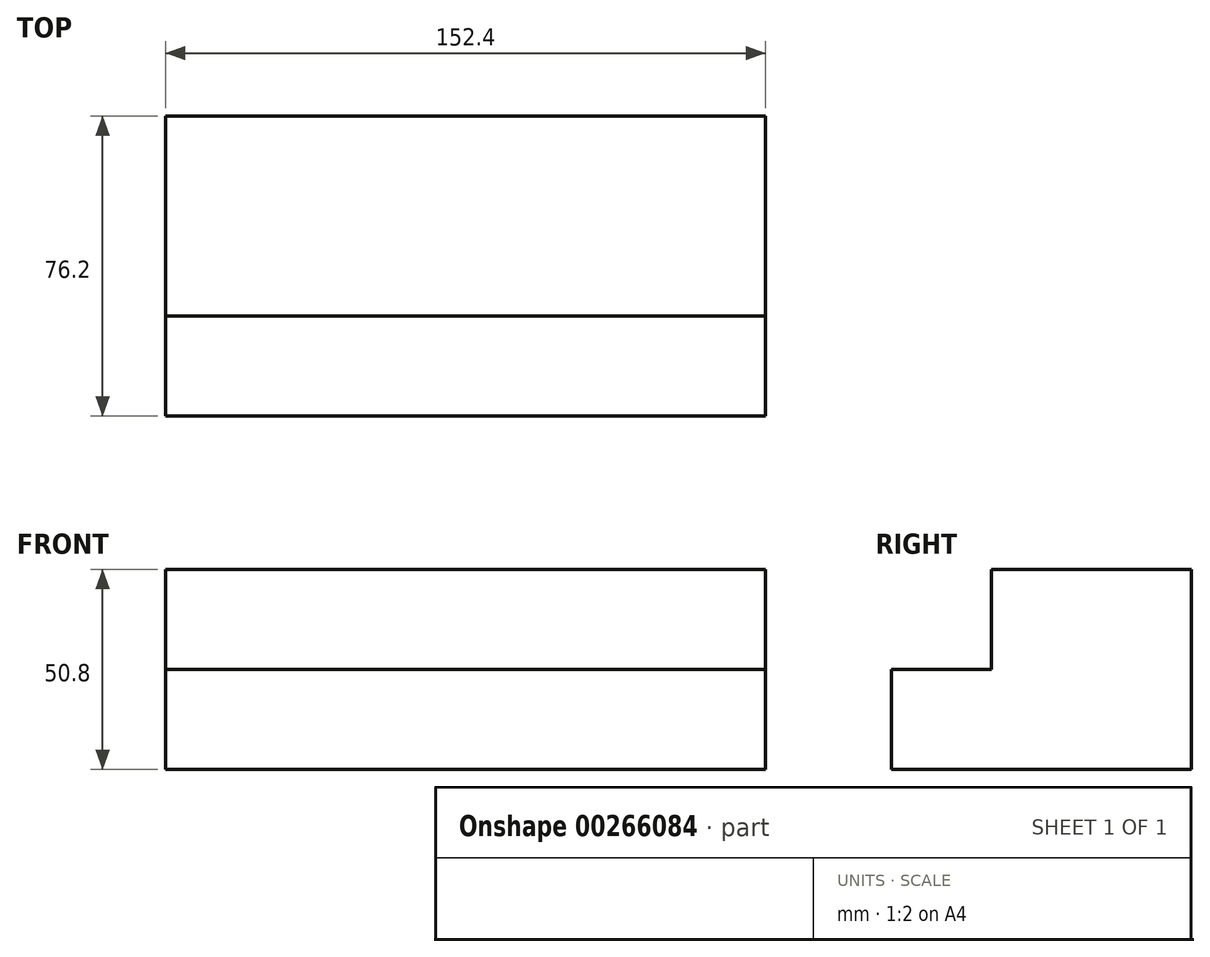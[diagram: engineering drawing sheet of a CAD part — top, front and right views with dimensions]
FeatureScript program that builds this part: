
annotation { "Feature Type Name" : "Feature", "Feature Type Description" : "" }
export const myFeature = defineFeature(function(context is Context, id is Id, definition is map)
    precondition{}
    {
        {
            var Q0;
            Q0=qCreatedBy(makeId("Right.planeOp"),FACE);
            var sketch = newSketch(context, id + "F0", { "sketchPlane" : qUnion([Q0])});
            skLineSegment(sketch, "E0.bottom", {"start": v(0, 0) * mm, "end": v(76.2, 0) * mm});
            skLineSegment(sketch, "E0.top", {"start": v(0, 50.8) * mm, "end": v(76.2, 50.8) * mm});
            skLineSegment(sketch, "E0.left", {"start": v(0, 0) * mm, "end": v(0, 50.8) * mm});
            skLineSegment(sketch, "E0.right", {"start": v(76.2, 0) * mm, "end": v(76.2, 50.8) * mm});
            skSolve(sketch);
        }
        {
            var Q0;
            Q0=makeQuery(id+"F0.imprint","IMPRINT",FACE,{"disambiguationData":[TD([[makeQuery(id+"F0.imprint","IMPRINT",EDGE,{"derivedFrom":sQuery(id+"F0.wireOp",EDGE,"E0.bottom")}),1.0]])]});
            extrude(context, id + "F1", {"entities" : qUnion([Q0]), "depth" : 152.4 * mm});
        }
        {
            var Q0;
            Q0=makeQuery(id+"F1.opExtrude","CAP_FACE",FACE,{"disambiguationData":[OSD([sQuery(id+"F0.wireOp",EDGE,"E0.bottom"),sQuery(id+"F0.wireOp",EDGE,"E0.top"),sQuery(id+"F0.wireOp",EDGE,"E0.left"),sQuery(id+"F0.wireOp",EDGE,"E0.right")])],"isStart":false});
            var sketch = newSketch(context, id + "F2", { "sketchPlane" : qUnion([Q0])});
            skLineSegment(sketch, "E1.bottom", {"start": v(0, 50.8) * mm, "end": v(25.4, 50.8) * mm});
            skLineSegment(sketch, "E1.top", {"start": v(0, 25.4) * mm, "end": v(25.4, 25.4) * mm});
            skLineSegment(sketch, "E1.left", {"start": v(0, 50.8) * mm, "end": v(0, 25.4) * mm});
            skLineSegment(sketch, "E1.right", {"start": v(25.4, 50.8) * mm, "end": v(25.4, 25.4) * mm});
            skSolve(sketch);
        }
        {
            var Q0;
            Q0=makeQuery(id+"F2.imprint","IMPRINT",FACE,{"disambiguationData":[TD([[makeQuery(id+"F2.imprint","IMPRINT",EDGE,{"derivedFrom":sQuery(id+"F2.wireOp",EDGE,"E1.bottom")}),-1.0]])]});
            extrude(context, id + "F3", {"entities" : qUnion([Q0]), "operationType" : NewBodyOperationType.ADD, "endBound" : BoundingType.UP_TO_NEXT, "oppositeDirection" : true, "depth" : 25.4 * mm});
        }
        {
            var Q0;
            Q0=makeQuery(id+"F1.opExtrude","CAP_FACE",FACE,{"disambiguationData":[OSD([sQuery(id+"F0.wireOp",EDGE,"E0.bottom"),sQuery(id+"F0.wireOp",EDGE,"E0.top"),sQuery(id+"F0.wireOp",EDGE,"E0.left"),sQuery(id+"F0.wireOp",EDGE,"E0.right")])],"isStart":false});
            var sketch = newSketch(context, id + "F4", { "sketchPlane" : qUnion([Q0])});
            skLineSegment(sketch, "E2.bottom", {"start": v(0, 50.8) * mm, "end": v(25.4, 50.8) * mm});
            skLineSegment(sketch, "E2.top", {"start": v(0, 25.4) * mm, "end": v(25.4, 25.4) * mm});
            skLineSegment(sketch, "E2.left", {"start": v(0, 50.8) * mm, "end": v(0, 25.4) * mm});
            skLineSegment(sketch, "E2.right", {"start": v(25.4, 50.8) * mm, "end": v(25.4, 25.4) * mm});
            skSolve(sketch);
        }
        {
            var Q0;
            Q0=makeQuery(id+"F4.imprint","IMPRINT",FACE,{"disambiguationData":[TD([[makeQuery(id+"F4.imprint","IMPRINT",EDGE,{"derivedFrom":sQuery(id+"F4.wireOp",EDGE,"E2.bottom")}),-1.0]])]});
            extrude(context, id + "F5", {"entities" : qUnion([Q0]), "operationType" : NewBodyOperationType.ADD, "oppositeDirection" : true, "depth" : 152.4 * mm});
        }
        {
            var Q0;
            Q0=makeQuery(id+"F1.opExtrude","CAP_FACE",FACE,{"disambiguationData":[OSD([sQuery(id+"F0.wireOp",EDGE,"E0.bottom"),sQuery(id+"F0.wireOp",EDGE,"E0.top"),sQuery(id+"F0.wireOp",EDGE,"E0.left"),sQuery(id+"F0.wireOp",EDGE,"E0.right")])],"isStart":false});
            var sketch = newSketch(context, id + "F6", { "sketchPlane" : qUnion([Q0])});
            skLineSegment(sketch, "E3.bottom", {"start": v(0, 50.8) * mm, "end": v(25.4, 50.8) * mm});
            skLineSegment(sketch, "E3.top", {"start": v(0, 25.4) * mm, "end": v(25.4, 25.4) * mm});
            skLineSegment(sketch, "E3.left", {"start": v(0, 50.8) * mm, "end": v(0, 25.4) * mm});
            skLineSegment(sketch, "E3.right", {"start": v(25.4, 50.8) * mm, "end": v(25.4, 25.4) * mm});
            skSolve(sketch);
        }
        {
            var Q0;
            Q0=makeQuery(id+"F6.imprint","IMPRINT",FACE,{"disambiguationData":[TD([[makeQuery(id+"F6.imprint","IMPRINT",EDGE,{"derivedFrom":sQuery(id+"F6.wireOp",EDGE,"E3.bottom")}),-1.0]])]});
            extrude(context, id + "F7", {"entities" : qUnion([Q0]), "operationType" : NewBodyOperationType.REMOVE, "oppositeDirection" : true, "depth" : 152.4 * mm});
        }
    });
